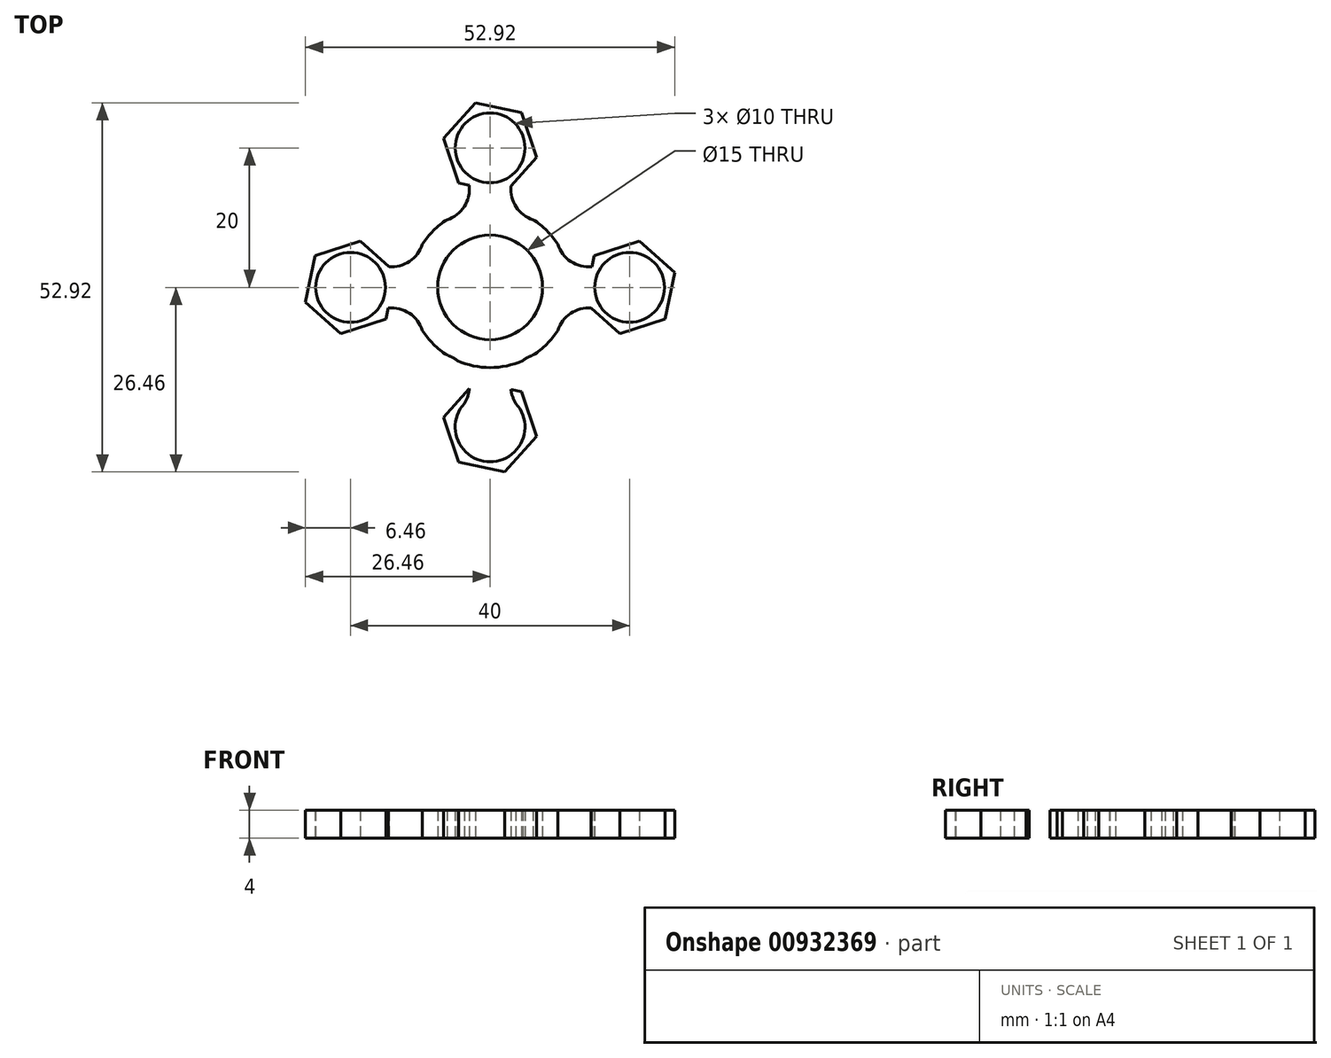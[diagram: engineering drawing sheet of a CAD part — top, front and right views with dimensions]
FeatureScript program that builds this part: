
annotation { "Feature Type Name" : "Feature", "Feature Type Description" : "" }
export const myFeature = defineFeature(function(context is Context, id is Id, definition is map)
    precondition{}
    {
        {
            var Q0;
            Q0=qCreatedBy(makeId("Top.planeOp"),FACE);
            var sketch = newSketch(context, id + "F0", { "sketchPlane" : qUnion([Q0])});
            skCircle(sketch, "E0", {"center": v(0, 0) * mm, "radius": 11.5 * mm});
            skCircle(sketch, "E1", {"center": v(0, 0) * mm, "radius": 7.5 * mm});
            skLineSegment(sketch, "E2", {"start": v(0, 0) * mm, "end": v(0, 20) * mm, "construction": true});
            skCircle(sketch, "E3", {"center": v(0, 20) * mm, "radius": 5 * mm});
            skArc(sketch, "E4", {"start": v(4.17, 17.25) * mm, "mid": v(3.11, 12.92) * mm, "end": v(6.18, 9.7) * mm});
            skArc(sketch, "E5.MirrorCS", {"start": v(-4.17, 17.25) * mm, "mid": v(-3.11, 12.92) * mm, "end": v(-6.18, 9.7) * mm});
            skCircle(sketch, "E6.cCircle", {"center": v(0, 20) * mm, "radius": 5.89 * mm, "construction": true});
            skLineSegment(sketch, "E6.1", {"start": v(-4.53, 14.93) * mm, "end": v(-6.65, 21.4) * mm});
            skLineSegment(sketch, "E6.2", {"start": v(-6.65, 21.4) * mm, "end": v(-2.12, 26.46) * mm});
            skLineSegment(sketch, "E6.3", {"start": v(-2.12, 26.46) * mm, "end": v(4.53, 25.07) * mm});
            skLineSegment(sketch, "E6.4", {"start": v(4.53, 25.07) * mm, "end": v(6.65, 18.6) * mm});
            skLineSegment(sketch, "E6.5", {"start": v(6.65, 18.6) * mm, "end": v(2.97, 14.5) * mm});
            skLineSegment(sketch, "E7.1.0", {"start": v(-26.46, -2.12) * mm, "end": v(-25.07, 4.53) * mm});
            skLineSegment(sketch, "E7.1.1", {"start": v(-25.07, 4.53) * mm, "end": v(-18.6, 6.65) * mm});
            skLineSegment(sketch, "E7.1.2", {"start": v(-18.6, 6.65) * mm, "end": v(-14.5, 2.97) * mm});
            skLineSegment(sketch, "E7.1.3", {"start": v(-14.61, -2.98) * mm, "end": v(-14.93, -4.53) * mm});
            skLineSegment(sketch, "E7.1.4", {"start": v(-14.93, -4.53) * mm, "end": v(-21.4, -6.65) * mm});
            skLineSegment(sketch, "E7.1.5", {"start": v(-21.4, -6.65) * mm, "end": v(-26.46, -2.12) * mm});
            skCircle(sketch, "E7.1.6", {"center": v(-20, 0) * mm, "radius": 5 * mm});
            skArc(sketch, "E7.1.7", {"start": v(-17.25, 4.17) * mm, "mid": v(-12.92, 3.11) * mm, "end": v(-9.7, 6.18) * mm});
            skArc(sketch, "E7.1.8", {"start": v(-17.25, -4.17) * mm, "mid": v(-12.92, -3.11) * mm, "end": v(-9.7, -6.18) * mm});
            skLineSegment(sketch, "E7.2.0", {"start": v(2.12, -26.46) * mm, "end": v(-4.53, -25.07) * mm});
            skLineSegment(sketch, "E7.2.1", {"start": v(-4.53, -25.07) * mm, "end": v(-6.65, -18.6) * mm});
            skLineSegment(sketch, "E7.2.2", {"start": v(-6.65, -18.6) * mm, "end": v(-2.97, -14.5) * mm});
            skLineSegment(sketch, "E7.2.3", {"start": v(2.98, -14.61) * mm, "end": v(4.53, -14.93) * mm});
            skLineSegment(sketch, "E7.2.4", {"start": v(4.53, -14.93) * mm, "end": v(6.65, -21.4) * mm});
            skLineSegment(sketch, "E7.2.5", {"start": v(6.65, -21.4) * mm, "end": v(2.12, -26.46) * mm});
            skCircle(sketch, "E7.2.6", {"center": v(0, -20) * mm, "radius": 5 * mm});
            skArc(sketch, "E7.2.7", {"start": v(-4.17, -17.25) * mm, "mid": v(-3.11, -12.92) * mm, "end": v(-6.18, -9.7) * mm});
            skArc(sketch, "E7.2.8", {"start": v(4.17, -17.25) * mm, "mid": v(3.11, -12.92) * mm, "end": v(6.18, -9.7) * mm});
            skLineSegment(sketch, "E7.3.0", {"start": v(26.46, 2.12) * mm, "end": v(25.07, -4.53) * mm});
            skLineSegment(sketch, "E7.3.1", {"start": v(25.07, -4.53) * mm, "end": v(18.6, -6.65) * mm});
            skLineSegment(sketch, "E7.3.2", {"start": v(18.6, -6.65) * mm, "end": v(14.5, -2.97) * mm});
            skLineSegment(sketch, "E7.3.3", {"start": v(14.61, 2.98) * mm, "end": v(14.93, 4.53) * mm});
            skLineSegment(sketch, "E7.3.4", {"start": v(14.93, 4.53) * mm, "end": v(21.4, 6.65) * mm});
            skLineSegment(sketch, "E7.3.5", {"start": v(21.4, 6.65) * mm, "end": v(26.46, 2.12) * mm});
            skCircle(sketch, "E7.3.6", {"center": v(20, 0) * mm, "radius": 5 * mm});
            skArc(sketch, "E7.3.7", {"start": v(17.25, -4.17) * mm, "mid": v(12.92, -3.11) * mm, "end": v(9.7, -6.18) * mm});
            skArc(sketch, "E7.3.8", {"start": v(17.25, 4.17) * mm, "mid": v(12.92, 3.11) * mm, "end": v(9.7, 6.18) * mm});
            skLineSegment(sketch, "E8.trimOffspring", {"start": v(-2.98, 14.61) * mm, "end": v(-4.53, 14.93) * mm});
            skSolve(sketch);
        }
        {
            var Q0;
            {var subQ0=sQuery(id+"F0.wireOp",EDGE,"E4");var subQ4=sQuery(id+"F0.wireOp",EDGE,"E0");var subQ5=makeQuery(id+"F0.imprint","INTERSECT",VERTEX,{"disambiguationData":[OD(1.0)],"derivedFrom":[subQ4,subQ0]});Q0=makeQuery(id+"F0.imprint","IMPRINT",FACE,{"disambiguationData":[TD([[makeQuery(id+"F0.imprint","IMPRINT",EDGE,{"disambiguationData":[TD([[subQ5,-1.0]])],"derivedFrom":subQ4}),-1.0]])]});}
            var Q1;
            Q1=makeQuery(id+"F0.imprint","IMPRINT",FACE,{"disambiguationData":[TD([[makeQuery(id+"F0.imprint","IMPRINT",EDGE,{"derivedFrom":sQuery(id+"F0.wireOp",EDGE,"E1")}),-1.0]])]});
            var Q2;
            {var subQ4=sQuery(id+"F0.wireOp",EDGE,"E7.3.8");var subQ5=sQuery(id+"F0.wireOp",EDGE,"E0");var subQ6=makeQuery(id+"F0.imprint","INTERSECT",VERTEX,{"disambiguationData":[OD(1.0)],"derivedFrom":[subQ5,subQ4]});Q2=makeQuery(id+"F0.imprint","IMPRINT",FACE,{"disambiguationData":[TD([[makeQuery(id+"F0.imprint","IMPRINT",EDGE,{"disambiguationData":[TD([[subQ6,1.0]])],"derivedFrom":subQ5}),-1.0]])]});}
            var Q3;
            {var subQ0=sQuery(id+"F0.wireOp",EDGE,"E7.2.7");var subQ4=sQuery(id+"F0.wireOp",EDGE,"E0");var subQ5=makeQuery(id+"F0.imprint","INTERSECT",VERTEX,{"disambiguationData":[OD(1.0)],"derivedFrom":[subQ4,subQ0]});Q3=makeQuery(id+"F0.imprint","IMPRINT",FACE,{"disambiguationData":[TD([[makeQuery(id+"F0.imprint","IMPRINT",EDGE,{"disambiguationData":[TD([[subQ5,-1.0]])],"derivedFrom":subQ4}),-1.0]])]});}
            var Q4;
            {var subQ0=sQuery(id+"F0.wireOp",EDGE,"E7.1.7");var subQ4=sQuery(id+"F0.wireOp",EDGE,"E0");var subQ5=makeQuery(id+"F0.imprint","INTERSECT",VERTEX,{"disambiguationData":[OD(1.0)],"derivedFrom":[subQ4,subQ0]});Q4=makeQuery(id+"F0.imprint","IMPRINT",FACE,{"disambiguationData":[TD([[makeQuery(id+"F0.imprint","IMPRINT",EDGE,{"disambiguationData":[TD([[subQ5,-1.0]])],"derivedFrom":subQ4}),-1.0]])]});}
            var Q5;
            Q5=makeQuery(id+"F0.imprint","IMPRINT",FACE,{"disambiguationData":[TD([[makeQuery(id+"F0.imprint","IMPRINT",EDGE,{"derivedFrom":sQuery(id+"F0.wireOp",EDGE,"E7.1.0")}),-1.0]])]});
            var Q6;
            Q6=makeQuery(id+"F0.imprint","IMPRINT",FACE,{"disambiguationData":[TD([[makeQuery(id+"F0.imprint","IMPRINT",EDGE,{"derivedFrom":sQuery(id+"F0.wireOp",EDGE,"E6.1")}),-1.0]])]});
            var Q7;
            Q7=makeQuery(id+"F0.imprint","IMPRINT",FACE,{"disambiguationData":[TD([[makeQuery(id+"F0.imprint","IMPRINT",EDGE,{"derivedFrom":sQuery(id+"F0.wireOp",EDGE,"E7.3.0")}),-1.0]])]});
            var Q8;
            Q8=makeQuery(id+"F0.imprint","IMPRINT",FACE,{"disambiguationData":[TD([[makeQuery(id+"F0.imprint","IMPRINT",EDGE,{"derivedFrom":sQuery(id+"F0.wireOp",EDGE,"E7.2.0")}),-1.0]])]});
            extrude(context, id + "F1", {"entities" : qUnion([Q0, Q1, Q2, Q3, Q4, Q5, Q6, Q7, Q8]), "depth" : 4 * mm, "offsetDistance" : 25 * mm});
        }
    });
